# Revit family: Sanitary_Showers_AXOR_36736CHN-AXOR-Citterio-E-Shower-bar-0-90_NEW
name_source: partatom
category: Plumbing Fixtures
revit_build: Autodesk Revit 2018 (Build: 20170223_1515(x64)
units: mm (PartAtom-declared; Revit-internal decimal feet)

## family parameters
Always vertical = No
Cut with Voids When Loaded = No
OmniClass Number = 23.31.17.00
OmniClass Title = Showers
Part Type = Normal
Room Calculation Point = No
Round Connector Dimension = Use Diameter
Shared = No
Work Plane-Based = Yes

## types (4) — shared parameters
Always visible = Yes
BIMobject category = Showers
Default Elevation = 1219.2 mm
Description = AXOR Citterio E Shower bar 0.90 m with shower hose 1.60 m
Design country = Germany
EAN code = 4059625433928
Edition number = 1
IFC Classification = Sanitary Terminal
Manufacturer = AXOR
Manufacturer country = Germany
Manufacturer name = AXOR
Material 2 = AXOR - Plastic - Gray
Material main = Brass
Material secondary = Chrome
Model = 36736CHN
OmniClass Code = 23-31 17 00
OmniClass Description = Showers
Product Guid = bb50652a-3296-4f30-9268-b715debd080f
Product SKU = 36736CHN
Product data url = https://bimobject.com
Product family = AXOR Citterio E
Product group = Wallbars
Product name = 36736CHN AXOR Citterio E Shower bar 0.90 m with shower hose 1.60 m
QR code = https://bimobject.com
URL = https://www.axor-design.com
Weight Net (Kg) = 3.3

## per-type parameters (varying)
| type | Material 1 |
| 007 Chrome | AXOR - Metal - 007 Chrome |
| 347 Brushed Black Chrome | AXOR - Metal - 347 Brushed Black Chrome |
| 677 Matt Black | AXOR - Metal - 677 Matt Black |
| 997 Polished Gold Optic | AXOR - Metal - 997 Polished Gold Optic |

## geometry (parser evidence)
native form markers: Sweep x1
no freeform markers — native parametric forms only
